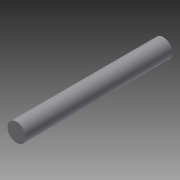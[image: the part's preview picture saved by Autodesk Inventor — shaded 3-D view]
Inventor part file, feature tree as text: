
AUTODESK INVENTOR PART (.ipt)
format: ipt  version: 2013 (Build 170138000, 138)  size: 68,096 bytes
history: native  units: in
note: dims shown in document units (in); Inventor stores cm internally (conversion verified against a paired STEP export)
features: extrude x1, sketch x1
ambient origin geometry x8: Origin, YZ Plane, XZ Plane, XY Plane, X Axis, Y Axis, Z Axis, Center Point
bodies: Solid1 (feature_tree)
feature tree (2):
  extrude  "Extrusion1"  Depth=1.5in TaperAngle=0.0deg
  sketch  "Sketch1"  dims[d0=0.1875in d3=1.5in d4=0.0in]
